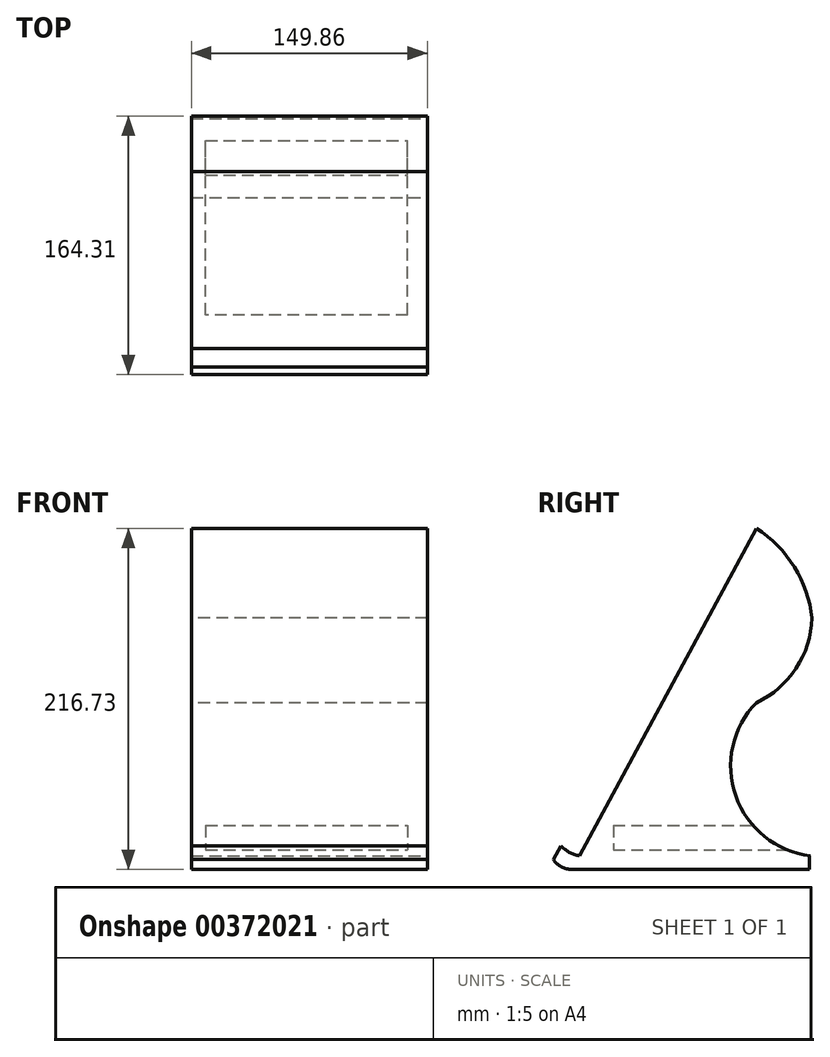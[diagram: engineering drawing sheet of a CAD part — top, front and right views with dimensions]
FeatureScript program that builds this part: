
annotation { "Feature Type Name" : "Feature", "Feature Type Description" : "" }
export const myFeature = defineFeature(function(context is Context, id is Id, definition is map)
    precondition{}
    {
        {
            var Q0;
            Q0=qCreatedBy(makeId("Right.planeOp"),FACE);
            var sketch = newSketch(context, id + "F0", { "sketchPlane" : qUnion([Q0])});
            skLineSegment(sketch, "E0", {"start": v(-72.94, -105.86) * mm, "end": v(44.24, 110.87) * mm});
            skLineSegment(sketch, "E1", {"start": v(-72.94, -105.86) * mm, "end": v(39.9, -105.86) * mm});
            skArc(sketch, "E2", {"start": v(79.54, 53.73) * mm, "mid": v(68.28, 86.25) * mm, "end": v(44.24, 110.87) * mm});
            skArc(sketch, "E3", {"start": v(44.24, 0) * mm, "mid": v(69.44, 21.9) * mm, "end": v(79.54, 53.73) * mm});
            skArc(sketch, "E4", {"start": v(44.24, 0) * mm, "mid": v(16.71, -18.7) * mm, "end": v(12.4, -51.7) * mm});
            skArc(sketch, "E5", {"start": v(12.4, -51.7) * mm, "mid": v(23.72, -80.01) * mm, "end": v(39.9, -105.86) * mm});
            skSolve(sketch);
        }
        {
            var Q0;
            Q0=makeQuery(id+"F0.imprint","IMPRINT",FACE,{"disambiguationData":[TD([[makeQuery(id+"F0.imprint","IMPRINT",EDGE,{"derivedFrom":sQuery(id+"F0.wireOp",EDGE,"E0")}),-1.0]])]});
            extrude(context, id + "F1", {"entities" : qUnion([Q0]), "depth" : 149.86 * mm});
        }
        {
            var Q0;
            Q0=makeQuery(id+"F1.opExtrude","CAP_FACE",FACE,{"disambiguationData":[OSD([sQuery(id+"F0.wireOp",EDGE,"E0"),sQuery(id+"F0.wireOp",EDGE,"E1"),sQuery(id+"F0.wireOp",EDGE,"E2"),sQuery(id+"F0.wireOp",EDGE,"E3"),sQuery(id+"F0.wireOp",EDGE,"E4"),sQuery(id+"F0.wireOp",EDGE,"E5")])],"isStart":false});
            var sketch = newSketch(context, id + "F2", { "sketchPlane" : qUnion([Q0])});
            skArc(sketch, "E6", {"start": v(-80.02, -90.74) * mm, "mid": v(-52, -92.29) * mm, "end": v(-50.45, -64.26) * mm});
            skLineSegment(sketch, "E7", {"start": v(-80.02, -90.74) * mm, "end": v(-84.77, -99.53) * mm});
            skArc(sketch, "E8", {"start": v(-84.77, -99.53) * mm, "mid": v(-79.65, -104.18) * mm, "end": v(-72.94, -105.86) * mm});
            skSolve(sketch);
        }
        {
            var Q0;
            {var subQ0=sQuery(id+"F2.wireOp",EDGE,"E6");Q0=makeQuery(id+"F2.imprint","IMPRINT",FACE,{"disambiguationData":[TD([[makeQuery(id+"F2.imprint","IMPRINT",EDGE,{"derivedFrom":subQ0}),-1.0]])]});}
            extrude(context, id + "F3", {"entities" : qUnion([Q0]), "operationType" : NewBodyOperationType.ADD, "oppositeDirection" : true, "depth" : 149.86 * mm});
        }
        {
            var Q0;
            {var subQ0=sQuery(id+"F0.wireOp",EDGE,"E0");Q0=makeQuery(id+"F3.boolean.opBoolean","MERGE",FACE,{"derivedFrom":[makeQuery(id+"F1.opExtrude","CAP_FACE",FACE,{"disambiguationData":[OSD([subQ0,sQuery(id+"F0.wireOp",EDGE,"E1"),sQuery(id+"F0.wireOp",EDGE,"E2"),sQuery(id+"F0.wireOp",EDGE,"E3"),sQuery(id+"F0.wireOp",EDGE,"E4"),sQuery(id+"F0.wireOp",EDGE,"E5")])],"isStart":false}),makeQuery(id+"F3.opExtrude","CAP_FACE",FACE,{"disambiguationData":[OSD([subQ0,sQuery(id+"F2.wireOp",EDGE,"E6"),sQuery(id+"F2.wireOp",EDGE,"E7"),sQuery(id+"F2.wireOp",EDGE,"E8")])],"isStart":true})]});}
            var sketch = newSketch(context, id + "F4", { "sketchPlane" : qUnion([Q0])});
            skLineSegment(sketch, "E9", {"start": v(-72.94, -105.86) * mm, "end": v(92.02, -105.86) * mm});
            skLineSegment(sketch, "E10", {"start": v(92.02, -105.86) * mm, "end": v(92.02, -97.12) * mm});
            skLineSegment(sketch, "E11", {"start": v(92.02, -97.12) * mm, "end": v(-68.22, -97.12) * mm});
            skLineSegment(sketch, "E12", {"start": v(-68.22, -97.12) * mm, "end": v(-72.94, -105.86) * mm});
            skArc(sketch, "E13", {"start": v(44.24, 0) * mm, "mid": v(33.74, -65.48) * mm, "end": v(92.02, -97.12) * mm});
            skSolve(sketch);
        }
        {
            var Q0;
            {var subQ5=makeQuery(id+"F1.opExtrude","CAP_EDGE",EDGE,{"disambiguationData":[OSD([sQuery(id+"F0.wireOp",EDGE,"E4")])],"isStart":false});Q0=makeQuery(id+"F4.imprint","IMPRINT",FACE,{"disambiguationData":[TD([[makeQuery(id+"F4.imprint","IMPRINT",EDGE,{"derivedFrom":subQ5}),1.0]])]});}
            extrude(context, id + "F5", {"entities" : qUnion([Q0]), "operationType" : NewBodyOperationType.ADD, "oppositeDirection" : true, "depth" : 149.86 * mm});
        }
        {
            var Q0;
            {var subQ0=sQuery(id+"F0.wireOp",EDGE,"E0");Q0=makeQuery(id+"F3.boolean.opBoolean","MERGE",FACE,{"derivedFrom":[makeQuery(id+"F1.opExtrude","CAP_FACE",FACE,{"disambiguationData":[OSD([subQ0,sQuery(id+"F0.wireOp",EDGE,"E1"),sQuery(id+"F0.wireOp",EDGE,"E2"),sQuery(id+"F0.wireOp",EDGE,"E3"),sQuery(id+"F0.wireOp",EDGE,"E4"),sQuery(id+"F0.wireOp",EDGE,"E5")])],"isStart":false}),makeQuery(id+"F3.opExtrude","CAP_FACE",FACE,{"disambiguationData":[OSD([subQ0,sQuery(id+"F2.wireOp",EDGE,"E6"),sQuery(id+"F2.wireOp",EDGE,"E7"),sQuery(id+"F2.wireOp",EDGE,"E8")])],"isStart":true})]});}
            var sketch = newSketch(context, id + "F6", { "sketchPlane" : qUnion([Q0])});
            skLineSegment(sketch, "E14", {"start": v(-68.22, -97.12) * mm, "end": v(-72.94, -105.86) * mm});
            skLineSegment(sketch, "E15", {"start": v(-72.94, -105.86) * mm, "end": v(78, -105.86) * mm});
            skLineSegment(sketch, "E16", {"start": v(78, -105.86) * mm, "end": v(78, -97.12) * mm});
            skLineSegment(sketch, "E17", {"start": v(78, -97.12) * mm, "end": v(-68.22, -97.12) * mm});
            skSolve(sketch);
        }
        {
            var Q0;
            {var subQ3=sQuery(id+"F6.wireOp",EDGE,"E16");Q0=makeQuery(id+"F6.imprint","IMPRINT",FACE,{"disambiguationData":[TD([[makeQuery(id+"F6.imprint","IMPRINT",EDGE,{"derivedFrom":subQ3}),1.0]])]});}
            extrude(context, id + "F7", {"entities" : qUnion([Q0]), "operationType" : NewBodyOperationType.ADD, "oppositeDirection" : true, "depth" : 149.86 * mm});
        }
        {
            var Q0;
            Q0=makeQuery(id+"F7.opExtrude","SWEPT_FACE",FACE,{"disambiguationData":[OSD([sQuery(id+"F6.wireOp",EDGE,"E16")])]});
            var sketch = newSketch(context, id + "F8", { "sketchPlane" : qUnion([Q0])});
            skLineSegment(sketch, "E18.bottom", {"start": v(-137.4, -77.85) * mm, "end": v(-9.06, -77.85) * mm});
            skLineSegment(sketch, "E18.top", {"start": v(-137.4, -93.48) * mm, "end": v(-9.06, -93.48) * mm});
            skLineSegment(sketch, "E18.left", {"start": v(-137.4, -77.85) * mm, "end": v(-137.4, -93.48) * mm});
            skLineSegment(sketch, "E18.right", {"start": v(-9.06, -77.85) * mm, "end": v(-9.06, -93.48) * mm});
            skSolve(sketch);
        }
        {
            var Q0;
            Q0=makeQuery(id+"F8.imprint","IMPRINT",FACE,{"disambiguationData":[TD([[makeQuery(id+"F8.imprint","IMPRINT",EDGE,{"derivedFrom":sQuery(id+"F8.wireOp",EDGE,"E18.bottom")}),-1.0]])]});
            extrude(context, id + "F9", {"entities" : qUnion([Q0]), "operationType" : NewBodyOperationType.REMOVE, "oppositeDirection" : true, "depth" : 124.7 * mm});
        }
    });
